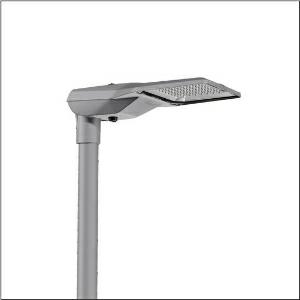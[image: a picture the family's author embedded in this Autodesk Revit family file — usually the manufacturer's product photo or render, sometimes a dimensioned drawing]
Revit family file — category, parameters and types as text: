
# Revit family: streetlight_sl_21_midi___st0_8a_5xe3c23t08lb_41e0
name_source: partatom
category: Lighting Fixtures
units: mm (PartAtom-declared; Revit-internal decimal feet)

## family parameters
Cut with Voids When Loaded = No
Host = Face
Light Source = No
Part Type = Normal
Room Calculation Point = No
Round Connector Dimension = Use Diameter
Shared = No

## types (1)
- --- (1 x LED, 11880 lm, 99.6 W, 2200K)
    Apparent Load = 100 VA
    CIE Flux Codes = 38 75 97 100 100
    Color Rendering = 70
    Color Temperature = 2200K
    Default Elevation = 1800 mm
    Description = Streetlight SL 21 midi, mast luminaire, primary light control with lens, of PMMA, primary optical cover: cover, of toughened safety glass, transparent, light distribution: ST0.8a, light emission: direct distribution, primary light characteristic: asymmetric, installation type: side-entry, post-top, LED, High Power LED, rated luminous flux: 11.880lm, luminous efficacy: 119lm/W, light colour: 722, colour temperature: 2200K, control gear: D4i, control: overheat protection, constant luminous flux control, time-dependent luminous flux control, flexible luminous flux parameterisation, pre-setting: logarithmic dimming characteristic, mains connection: 230..240V, AC, 50/60Hz, start of lifetime: 100W, end of service life: 102W, reduction: 45W, luminaire housing, of diecast aluminium, powder-coated, Siteco® metallic grey (DB 702S), corrosivity category C5 mid according to DIN EN ISO 12944, please order mast flange separately, inclination adjustable: 0°, 5°, 10°, 15°, sealing non-destructively replaceable, multi-level sealing system, length: 644mm, width: 335mm, height: 110mm, mast flange for spigot size: 42mm (side-entry): 5XC10008XM4, 60/48mm (side-entry/post-top): 5XC10108XM2, 76/60mm (side-entry/post-top): 5XC10108XM1, mounting height: 4..8m, Smart Interface below and above, protection rating (complete): IP66, insulation class (complete): insulation class II (safety insulation), certification: CE, ENEC, ENEC+, VDE, impact resistance: IK10, permissible operating ambient temperature for outdoor applications: -40..+50°C, standard-compliant lighting for roads and squares, packaging unit: 1 piece

Light Distribution: ST0.8a
    Height = 111 mm
    Lamp = 1 x LED
    Lamp Light Flux = 11880 lm
    Lamp Power = 99.6 W
    Lamp count = 1
    Length = 644 mm
    Luminous efficacy = 119 lm/W
    Manufacturer = Siteco
    ModVariant = No
    Model = 5XE3C23T08LB
    Number of Poles = 1
    OnlyDefault = Yes
    Power Factor = 1
    Product Name = Streetlight SL 21 midi | ST0.8a
    Product group = mast luminaire | pylon top
    ProductGroupID = 6100
    Protection Class = Protection class II
    Protection Degree = IP 66
    RLX_Detail_Level = 1
    RLX_Emergency_Light_Flux = 0 lm
    RLX_Emergency_Type = 0
    RLX_Emergency_Type_DB = No
    RlxData = <blob elided: 27017 chars, md5=823dc631>
    Socket = socket
    Standby Power = 0 W
    System Light Flux = 11880 lm
    System Power = 100 W
    Type Comments = factory setting: luminous flux: 100 % | dim-lin: 254 | 1020 mA
    Type Image = l_1004304.jpg
    URL = http://relux.com
    VarID = @adj_011415
    Voltage = 0 V
    Weight = 0.00 kg
    Width = 336 mm

## geometry (parser evidence)
native form markers: Blend x4, Sweep x10
no freeform markers — native parametric forms only
